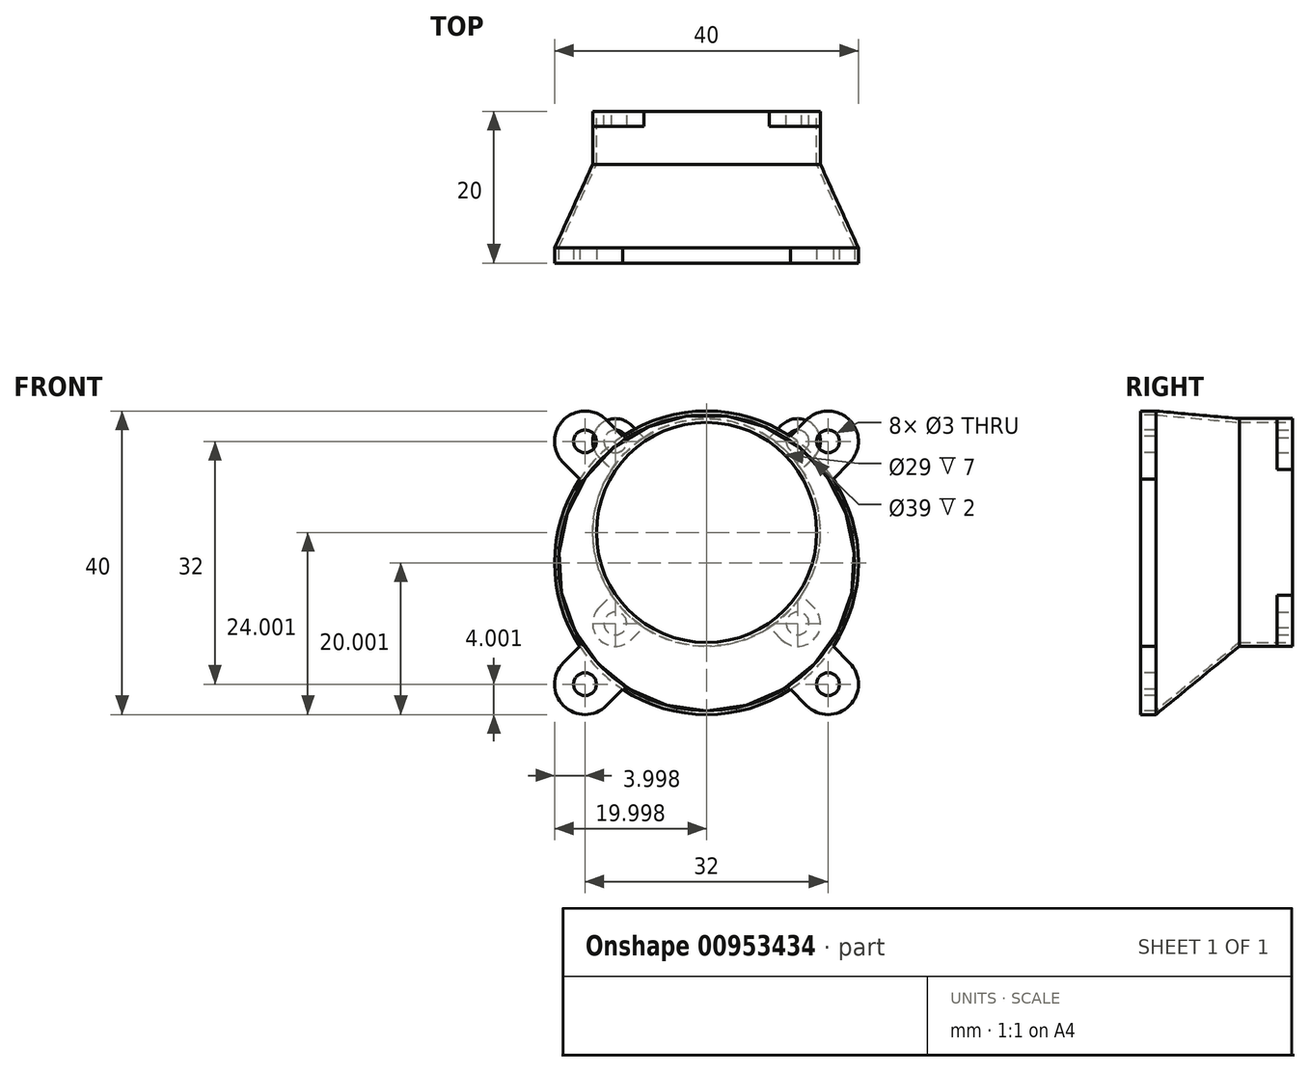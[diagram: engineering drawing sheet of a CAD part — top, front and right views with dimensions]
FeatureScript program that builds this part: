
annotation { "Feature Type Name" : "Feature", "Feature Type Description" : "" }
export const myFeature = defineFeature(function(context is Context, id is Id, definition is map)
    precondition{}
    {
        {
            var Q0;
            Q0=qCreatedBy(makeId("Front.planeOp"),FACE);
            cPlane(context, id + "F0", {"entities" : qUnion([Q0]), "cplaneType" : CPlaneType.OFFSET, "offset" : 5 * mm, "width" : 150 * mm, "height" : 150 * mm});
        }
        {
            var Q0;
            Q0=qCreatedBy(makeId("Front.planeOp"),FACE);
            cPlane(context, id + "F1", {"entities" : qUnion([Q0]), "cplaneType" : CPlaneType.OFFSET, "offset" : 25 * mm, "width" : 150 * mm, "height" : 150 * mm});
        }
        {
            var Q0;
            Q0=qCreatedBy(id+"F0.planeOp",FACE);
            var sketch = newSketch(context, id + "F2", { "sketchPlane" : qUnion([Q0])});
            skLineSegment(sketch, "E0.bottom", {"start": v(-75.62, 11.98) * mm, "end": v(-45.62, 11.98) * mm, "construction": true});
            skLineSegment(sketch, "E0.top", {"start": v(-75.62, -18.02) * mm, "end": v(-45.62, -18.02) * mm, "construction": true});
            skLineSegment(sketch, "E0.left", {"start": v(-75.62, 11.98) * mm, "end": v(-75.62, -18.02) * mm, "construction": true});
            skLineSegment(sketch, "E0.right", {"start": v(-45.62, 11.98) * mm, "end": v(-45.62, -18.02) * mm, "construction": true});
            skCircle(sketch, "E1", {"center": v(-72.62, 8.98) * mm, "radius": 1.5 * mm, "construction": true});
            skLineSegment(sketch, "E2", {"start": v(-60.62, 24.6) * mm, "end": v(-60.62, -27.9) * mm, "construction": true});
            skLineSegment(sketch, "E3", {"start": v(-85.98, -3.02) * mm, "end": v(-31.21, -3.02) * mm, "construction": true});
            skCircle(sketch, "E4.MirrorC", {"center": v(-48.62, 8.98) * mm, "radius": 1.5 * mm, "construction": true});
            skCircle(sketch, "E5.MirrorC", {"center": v(-48.62, -15.02) * mm, "radius": 1.5 * mm, "construction": true});
            skCircle(sketch, "E6.MirrorC", {"center": v(-72.62, -15.02) * mm, "radius": 1.5 * mm, "construction": true});
            skCircle(sketch, "E7", {"center": v(-60.62, -3.02) * mm, "radius": 14.5 * mm, "construction": true});
            skCircle(sketch, "E8", {"center": v(-60.62, -3.02) * mm, "radius": 15 * mm, "construction": true});
            skSolve(sketch);
        }
        {
            var Q0;
            Q0=qCreatedBy(id+"F1.planeOp",FACE);
            var sketch = newSketch(context, id + "F3", { "sketchPlane" : qUnion([Q0])});
            skCircle(sketch, "E9", {"center": v(-60.62, -7.02) * mm, "radius": 20 * mm, "construction": true});
            skLineSegment(sketch, "E10.bottom", {"start": v(-80.62, 12.98) * mm, "end": v(-40.62, 12.98) * mm, "construction": true});
            skLineSegment(sketch, "E10.top", {"start": v(-80.62, -27.02) * mm, "end": v(-40.62, -27.02) * mm, "construction": true});
            skLineSegment(sketch, "E10.left", {"start": v(-80.62, 12.98) * mm, "end": v(-80.62, -27.02) * mm, "construction": true});
            skLineSegment(sketch, "E10.right", {"start": v(-40.62, 12.98) * mm, "end": v(-40.62, -27.02) * mm, "construction": true});
            skCircle(sketch, "E11", {"center": v(-76.62, 8.98) * mm, "radius": 1.5 * mm, "construction": true});
            skLineSegment(sketch, "E12", {"start": v(-60.62, 28.38) * mm, "end": v(-60.62, -42.79) * mm, "construction": true});
            skLineSegment(sketch, "E13", {"start": v(-88.68, -7.02) * mm, "end": v(-31.75, -7.02) * mm, "construction": true});
            skCircle(sketch, "E14.MirrorC", {"center": v(-44.62, 8.98) * mm, "radius": 1.5 * mm, "construction": true});
            skCircle(sketch, "E15.MirrorC", {"center": v(-44.62, -23.02) * mm, "radius": 1.5 * mm, "construction": true});
            skCircle(sketch, "E16.MirrorC", {"center": v(-76.62, -23.02) * mm, "radius": 1.5 * mm, "construction": true});
            skCircle(sketch, "E17", {"center": v(-60.62, -7.02) * mm, "radius": 19.5 * mm, "construction": true});
            skSolve(sketch);
        }
        {
            var Q0;
            Q0=qCreatedBy(id+"F0.planeOp",FACE);
            var sketch = newSketch(context, id + "F4", { "sketchPlane" : qUnion([Q0])});
            skCircle(sketch, "E18", {"center": v(-60.62, -3.02) * mm, "radius": 14.5 * mm});
            skCircle(sketch, "E19", {"center": v(-72.62, 8.98) * mm, "radius": 1.5 * mm});
            skCircle(sketch, "E20", {"center": v(-48.62, 8.98) * mm, "radius": 1.5 * mm});
            skCircle(sketch, "E21", {"center": v(-48.62, -15.02) * mm, "radius": 1.5 * mm});
            skCircle(sketch, "E22", {"center": v(-72.62, -15.02) * mm, "radius": 1.5 * mm});
            skCircle(sketch, "E23", {"center": v(-72.62, 8.98) * mm, "radius": 3 * mm, "construction": true});
            skCircle(sketch, "E24", {"center": v(-48.62, 8.98) * mm, "radius": 3 * mm, "construction": true});
            skCircle(sketch, "E25", {"center": v(-48.62, -15.02) * mm, "radius": 3 * mm, "construction": true});
            skCircle(sketch, "E26", {"center": v(-72.62, -15.02) * mm, "radius": 3 * mm, "construction": true});
            skLineSegment(sketch, "E27", {"start": v(-70.5, 11.1) * mm, "end": v(-46.5, -12.9) * mm, "construction": true});
            skLineSegment(sketch, "E28", {"start": v(-74.74, 6.86) * mm, "end": v(-50.74, -17.14) * mm, "construction": true});
            skLineSegment(sketch, "E29", {"start": v(-50.74, 11.1) * mm, "end": v(-74.74, -12.9) * mm, "construction": true});
            skLineSegment(sketch, "E30", {"start": v(-70.5, -17.14) * mm, "end": v(-46.5, 6.86) * mm, "construction": true});
            skLineSegment(sketch, "E31", {"start": v(-68.53, 9.13) * mm, "end": v(-70.5, 11.1) * mm});
            skLineSegment(sketch, "E32", {"start": v(-74.74, 6.86) * mm, "end": v(-72.77, 4.9) * mm});
            skLineSegment(sketch, "E33", {"start": v(-52.71, 9.13) * mm, "end": v(-50.74, 11.1) * mm});
            skLineSegment(sketch, "E34", {"start": v(-46.5, 6.86) * mm, "end": v(-48.47, 4.9) * mm});
            skLineSegment(sketch, "E35", {"start": v(-46.5, -12.9) * mm, "end": v(-48.47, -10.93) * mm});
            skLineSegment(sketch, "E36", {"start": v(-50.74, -17.14) * mm, "end": v(-52.71, -15.17) * mm});
            skLineSegment(sketch, "E37", {"start": v(-70.5, -17.14) * mm, "end": v(-68.53, -15.17) * mm});
            skLineSegment(sketch, "E38", {"start": v(-74.74, -12.9) * mm, "end": v(-72.77, -10.93) * mm});
            skArc(sketch, "E39", {"start": v(-74.74, -12.9) * mm, "mid": v(-74.74, -17.14) * mm, "end": v(-70.5, -17.14) * mm});
            skArc(sketch, "E40", {"start": v(-50.74, -17.14) * mm, "mid": v(-46.5, -17.14) * mm, "end": v(-46.5, -12.9) * mm});
            skArc(sketch, "E41", {"start": v(-50.74, 11.1) * mm, "mid": v(-46.5, 11.1) * mm, "end": v(-46.5, 6.86) * mm});
            skArc(sketch, "E42", {"start": v(-70.5, 11.1) * mm, "mid": v(-74.74, 11.1) * mm, "end": v(-74.74, 6.86) * mm});
            skCircle(sketch, "E43", {"center": v(-60.62, -3.02) * mm, "radius": 15 * mm});
            skSolve(sketch);
        }
        {
            var Q0;
            Q0=qCreatedBy(id+"F1.planeOp",FACE);
            var sketch = newSketch(context, id + "F5", { "sketchPlane" : qUnion([Q0])});
            skCircle(sketch, "E44", {"center": v(-60.62, -7.02) * mm, "radius": 19.5 * mm});
            skCircle(sketch, "E45", {"center": v(-60.62, -7.02) * mm, "radius": 20 * mm});
            skCircle(sketch, "E46", {"center": v(-76.62, -23.02) * mm, "radius": 1.5 * mm});
            skCircle(sketch, "E47", {"center": v(-76.62, 8.98) * mm, "radius": 1.5 * mm});
            skCircle(sketch, "E48", {"center": v(-44.62, 8.98) * mm, "radius": 1.5 * mm});
            skCircle(sketch, "E49", {"center": v(-44.62, -23.02) * mm, "radius": 1.5 * mm});
            skCircle(sketch, "E50", {"center": v(-76.62, 8.98) * mm, "radius": 4 * mm, "construction": true});
            skCircle(sketch, "E51", {"center": v(-44.62, -23.02) * mm, "radius": 4 * mm, "construction": true});
            skLineSegment(sketch, "E52", {"start": v(-79.45, 6.15) * mm, "end": v(-47.45, -25.85) * mm, "construction": true});
            skLineSegment(sketch, "E53", {"start": v(-73.8, 11.8) * mm, "end": v(-41.8, -20.2) * mm, "construction": true});
            skArc(sketch, "E54", {"start": v(-73.8, 11.8) * mm, "mid": v(-79.45, 11.8) * mm, "end": v(-79.45, 6.15) * mm});
            skLineSegment(sketch, "E55", {"start": v(-79.45, 6.15) * mm, "end": v(-77.3, 4) * mm});
            skLineSegment(sketch, "E56", {"start": v(-73.8, 11.8) * mm, "end": v(-71.65, 9.67) * mm});
            skArc(sketch, "E57.MirrorCS", {"start": v(-47.45, 11.8) * mm, "mid": v(-41.8, 11.8) * mm, "end": v(-41.8, 6.15) * mm});
            skLineSegment(sketch, "E58.MirrorCS", {"start": v(-47.45, 11.8) * mm, "end": v(-49.6, 9.67) * mm});
            skLineSegment(sketch, "E59.MirrorCS", {"start": v(-41.8, 6.15) * mm, "end": v(-43.94, 4) * mm});
            skLineSegment(sketch, "E60.MirrorCS", {"start": v(-79.45, -20.2) * mm, "end": v(-77.3, -18.05) * mm});
            skLineSegment(sketch, "E61.MirrorCS", {"start": v(-73.8, -25.85) * mm, "end": v(-71.65, -23.7) * mm});
            skArc(sketch, "E62.MirrorCS", {"start": v(-73.8, -25.85) * mm, "mid": v(-79.45, -25.85) * mm, "end": v(-79.45, -20.2) * mm});
            skLineSegment(sketch, "E63.MirrorCS", {"start": v(-47.45, -25.85) * mm, "end": v(-49.6, -23.7) * mm});
            skArc(sketch, "E64.MirrorCS", {"start": v(-47.45, -25.85) * mm, "mid": v(-41.8, -25.85) * mm, "end": v(-41.8, -20.2) * mm});
            skLineSegment(sketch, "E65.MirrorCS", {"start": v(-41.8, -20.2) * mm, "end": v(-43.94, -18.05) * mm});
            skSolve(sketch);
        }
        {
            var Q0;
            Q0=qCreatedBy(id+"F0.planeOp",FACE);
            cPlane(context, id + "F6", {"entities" : qUnion([Q0]), "cplaneType" : CPlaneType.OFFSET, "offset" : 2 * mm, "width" : 150 * mm, "height" : 150 * mm});
        }
        {
            var Q0;
            Q0=qCreatedBy(id+"F6.planeOp",FACE);
            var sketch = newSketch(context, id + "F7", { "sketchPlane" : qUnion([Q0])});
            skCircle(sketch, "E66", {"center": v(-60.62, -3.02) * mm, "radius": 14.5 * mm});
            skCircle(sketch, "E67", {"center": v(-60.62, -3.02) * mm, "radius": 15 * mm});
            skSolve(sketch);
        }
        {
            var Q0;
            Q0=qCreatedBy(id+"F6.planeOp",FACE);
            cPlane(context, id + "F8", {"entities" : qUnion([Q0]), "cplaneType" : CPlaneType.OFFSET, "offset" : 5 * mm, "width" : 150 * mm, "height" : 150 * mm});
        }
        {
            var Q0;
            Q0 = qSketchRegion(id + "F4", true);
            var Q1;
            Q1=qCreatedBy(id+"F6.planeOp",FACE);
            extrude(context, id + "F9", {"entities" : qUnion([Q0]), "endBound" : BoundingType.UP_TO_SURFACE, "depth" : 10 * mm, "endBoundEntityFace" : qUnion([Q1]), "offsetDistance" : 25 * mm});
        }
        {
            var Q0;
            Q0 = qSketchRegion(id + "F7", true);
            var Q1;
            Q1=qCreatedBy(id+"F8.planeOp",FACE);
            extrude(context, id + "F10", {"entities" : qUnion([Q0]), "operationType" : NewBodyOperationType.ADD, "endBound" : BoundingType.UP_TO_SURFACE, "depth" : 25 * mm, "endBoundEntityFace" : qUnion([Q1]), "offsetDistance" : 25 * mm});
        }
        {
            var Q0;
            Q0=qCreatedBy(id+"F8.planeOp",FACE);
            var sketch = newSketch(context, id + "F11", { "sketchPlane" : qUnion([Q0])});
            skCircle(sketch, "E68", {"center": v(-60.62, -3.02) * mm, "radius": 15 * mm});
            skSolve(sketch);
        }
        {
            var Q0;
            Q0=qCreatedBy(id+"F8.planeOp",FACE);
            var sketch = newSketch(context, id + "F12", { "sketchPlane" : qUnion([Q0])});
            skCircle(sketch, "E69", {"center": v(-60.62, -3.02) * mm, "radius": 14.5 * mm});
            skSolve(sketch);
        }
        {
            var Q0;
            Q0=qCreatedBy(id+"F1.planeOp",FACE);
            cPlane(context, id + "F13", {"entities" : qUnion([Q0]), "cplaneType" : CPlaneType.OFFSET, "offset" : 2 * mm, "oppositeDirection" : true, "width" : 150 * mm, "height" : 150 * mm});
        }
        {
            var Q0;
            Q0=qCreatedBy(id+"F13.planeOp",FACE);
            var sketch = newSketch(context, id + "F14", { "sketchPlane" : qUnion([Q0])});
            skCircle(sketch, "E70", {"center": v(-60.62, -7.02) * mm, "radius": 20 * mm});
            skSolve(sketch);
        }
        {
            var Q0;
            Q0=qCreatedBy(id+"F13.planeOp",FACE);
            var sketch = newSketch(context, id + "F15", { "sketchPlane" : qUnion([Q0])});
            skCircle(sketch, "E71", {"center": v(-60.62, -7.02) * mm, "radius": 19.5 * mm});
            skSolve(sketch);
        }
        {
            var Q1;
            Q1=makeQuery(id+"F11.imprint","IMPRINT",FACE,{"disambiguationData":[TD([[makeQuery(id+"F11.imprint","IMPRINT",EDGE,{"derivedFrom":sQuery(id+"F11.wireOp",EDGE,"E68")}),1.0]])]});
            var Q2;
            Q2=makeQuery(id+"F14.imprint","IMPRINT",FACE,{"disambiguationData":[TD([[makeQuery(id+"F14.imprint","IMPRINT",EDGE,{"derivedFrom":sQuery(id+"F14.wireOp",EDGE,"E70")}),1.0]])]});
            loft(context, id + "F16", {"operationType" : NewBodyOperationType.ADD, "sheetProfilesArray" : [{ "sheetProfileEntities" : qUnion([Q1]) }, { "sheetProfileEntities" : qUnion([Q2]) }]});
        }
        {
            var Q1;
            Q1=makeQuery(id+"F12.imprint","IMPRINT",FACE,{"disambiguationData":[TD([[makeQuery(id+"F12.imprint","IMPRINT",EDGE,{"derivedFrom":sQuery(id+"F12.wireOp",EDGE,"E69")}),1.0]])]});
            var Q2;
            Q2=makeQuery(id+"F15.imprint","IMPRINT",FACE,{"disambiguationData":[TD([[makeQuery(id+"F15.imprint","IMPRINT",EDGE,{"derivedFrom":sQuery(id+"F15.wireOp",EDGE,"E71")}),1.0]])]});
            loft(context, id + "F17", {"operationType" : NewBodyOperationType.REMOVE, "sheetProfilesArray" : [{ "sheetProfileEntities" : qUnion([Q1]) }, { "sheetProfileEntities" : qUnion([Q2]) }]});
        }
        {
            var Q0;
            Q0 = qSketchRegion(id + "F5", true);
            var Q1;
            Q1=qCreatedBy(id+"F13.planeOp",FACE);
            extrude(context, id + "F18", {"entities" : qUnion([Q0]), "operationType" : NewBodyOperationType.ADD, "endBound" : BoundingType.UP_TO_SURFACE, "oppositeDirection" : true, "depth" : 25 * mm, "endBoundEntityFace" : qUnion([Q1]), "offsetDistance" : 25 * mm});
        }
    });
